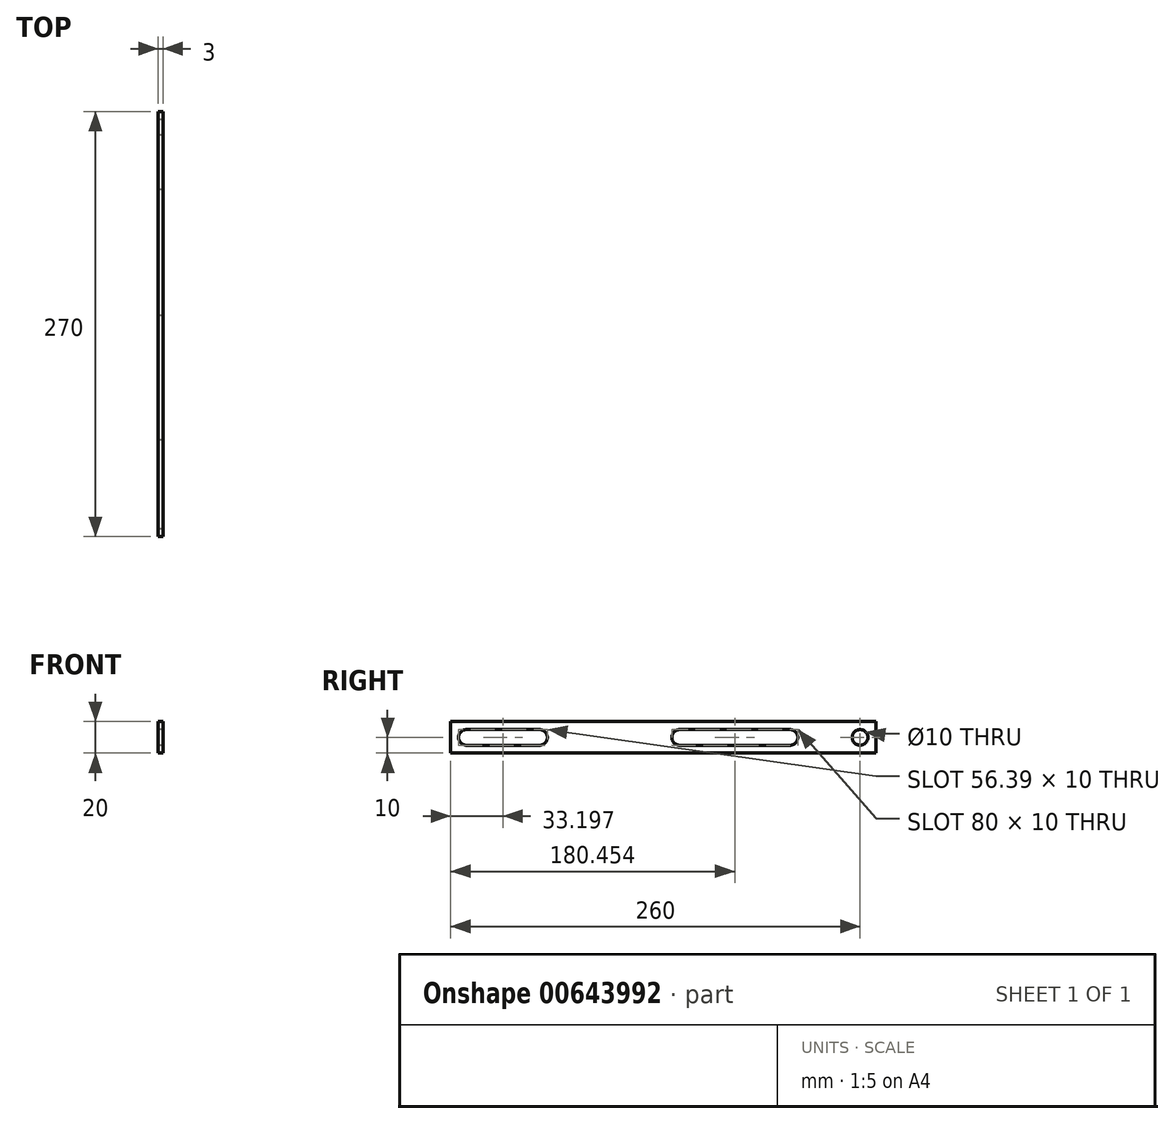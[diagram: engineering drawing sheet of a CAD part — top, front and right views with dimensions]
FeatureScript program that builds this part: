
annotation { "Feature Type Name" : "Feature", "Feature Type Description" : "" }
export const myFeature = defineFeature(function(context is Context, id is Id, definition is map)
    precondition{}
    {
        {
            var Q0;
            Q0=qCreatedBy(makeId("Right.planeOp"),FACE);
            var sketch = newSketch(context, id + "F0", { "sketchPlane" : qUnion([Q0])});
            skLineSegment(sketch, "E0", {"start": v(0, 0) * mm, "end": v(0, 20) * mm});
            skLineSegment(sketch, "E1", {"start": v(0, 20) * mm, "end": v(270, 20) * mm});
            skLineSegment(sketch, "E2", {"start": v(270, 20) * mm, "end": v(270, 0) * mm});
            skLineSegment(sketch, "E3", {"start": v(270, 0) * mm, "end": v(0, 0) * mm});
            skCircle(sketch, "E4", {"center": v(10, 10) * mm, "radius": 5 * mm});
            skCircle(sketch, "E5", {"center": v(56.4, 10) * mm, "radius": 5 * mm});
            skLineSegment(sketch, "E6", {"start": v(10, 15) * mm, "end": v(56.4, 15) * mm});
            skLineSegment(sketch, "E7", {"start": v(10, 5) * mm, "end": v(56.4, 5) * mm});
            skCircle(sketch, "E8", {"center": v(260, 10) * mm, "radius": 5 * mm});
            skCircle(sketch, "E9", {"center": v(145.45, 10) * mm, "radius": 5 * mm});
            skCircle(sketch, "E10", {"center": v(215.45, 10) * mm, "radius": 5 * mm});
            skLineSegment(sketch, "E11", {"start": v(145.45, 15) * mm, "end": v(215.45, 15) * mm});
            skLineSegment(sketch, "E12", {"start": v(215.45, 5) * mm, "end": v(145.45, 5) * mm});
            skSolve(sketch);
        }
        {
            var Q0;
            Q0=makeQuery(id+"F0.imprint","IMPRINT",FACE,{"disambiguationData":[TD([[makeQuery(id+"F0.imprint","IMPRINT",EDGE,{"derivedFrom":sQuery(id+"F0.wireOp",EDGE,"E0")}),-1.0]])]});
            extrude(context, id + "F1", {"entities" : qUnion([Q0]), "depth" : 3 * mm, "offsetDistance" : 25 * mm});
        }
    });
